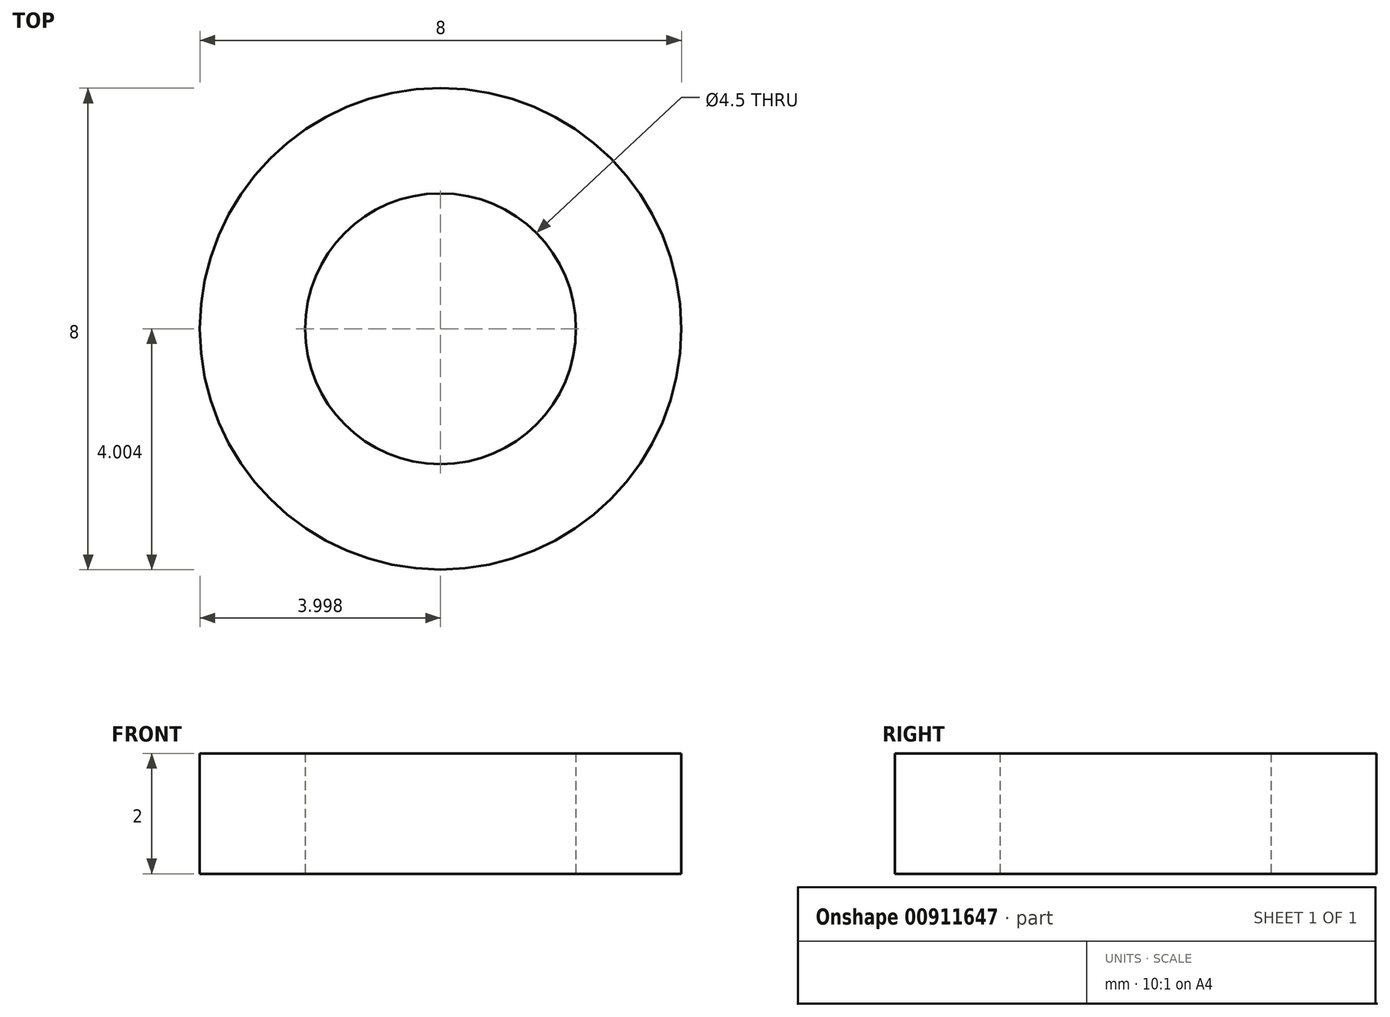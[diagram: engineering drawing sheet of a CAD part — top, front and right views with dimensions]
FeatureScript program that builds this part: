
annotation { "Feature Type Name" : "Feature", "Feature Type Description" : "" }
export const myFeature = defineFeature(function(context is Context, id is Id, definition is map)
    precondition{}
    {
        {
            var Q0;
            Q0=qCreatedBy(makeId("Top.planeOp"),FACE);
            var sketch = newSketch(context, id + "F0", { "sketchPlane" : qUnion([Q0])});
            skCircle(sketch, "E0", {"center": v(-20.04, 3.43) * mm, "radius": 2.25 * mm});
            skCircle(sketch, "E1", {"center": v(-20.04, 3.43) * mm, "radius": 4 * mm});
            skSolve(sketch);
        }
        {
            var Q0;
            Q0=makeQuery(id+"F0.imprint","IMPRINT",FACE,{"disambiguationData":[TD([[makeQuery(id+"F0.imprint","IMPRINT",EDGE,{"derivedFrom":sQuery(id+"F0.wireOp",EDGE,"E0")}),-1.0]])]});
            extrude(context, id + "F1", {"entities" : qUnion([Q0]), "depth" : 2 * mm, "offsetDistance" : 25.4 * mm});
        }
    });
